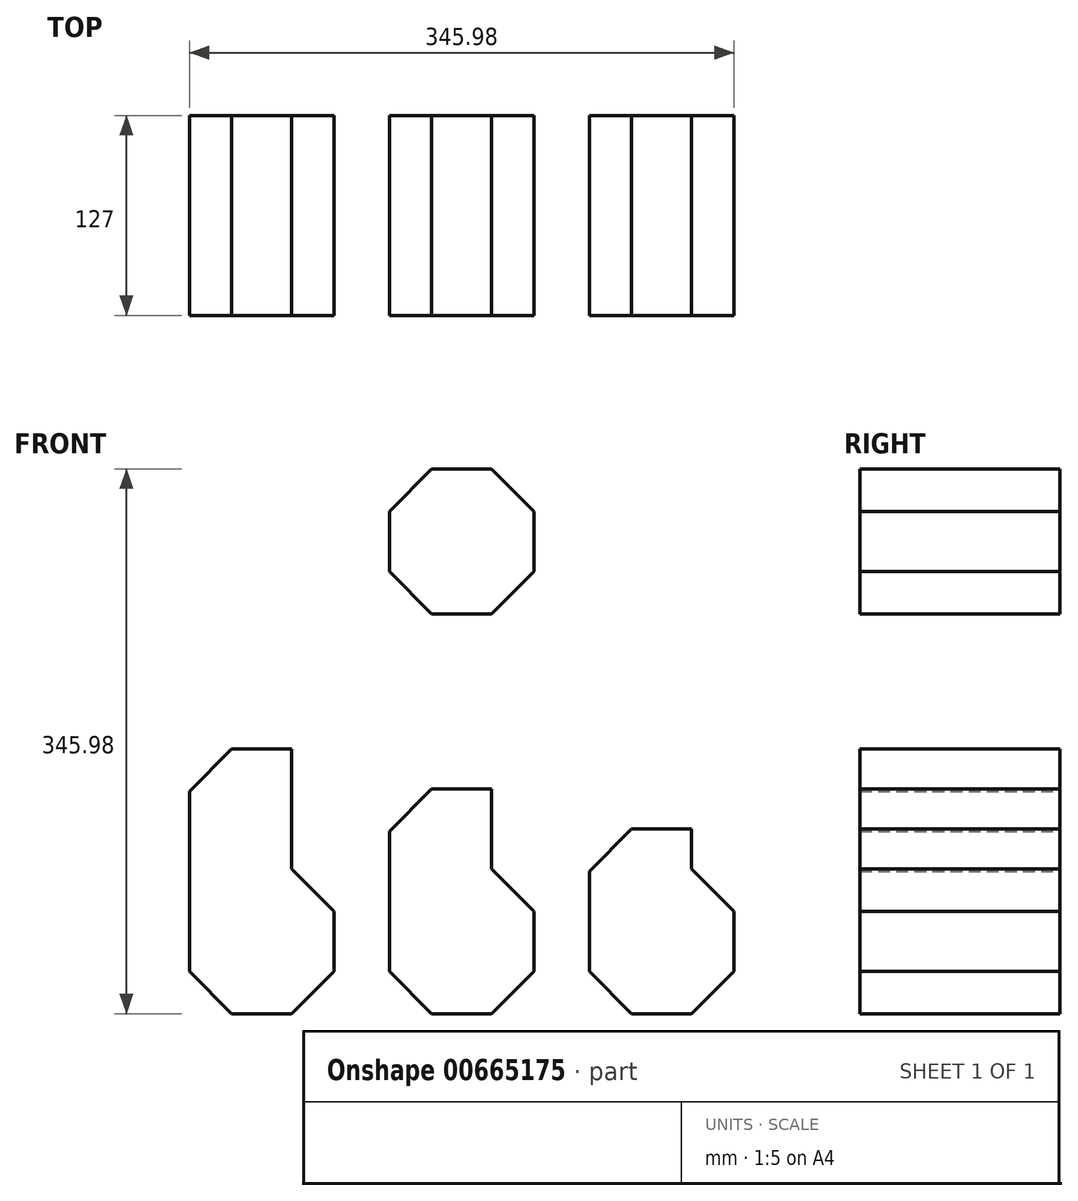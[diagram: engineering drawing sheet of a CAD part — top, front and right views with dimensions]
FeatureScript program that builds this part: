
annotation { "Feature Type Name" : "Feature", "Feature Type Description" : "" }
export const myFeature = defineFeature(function(context is Context, id is Id, definition is map)
    precondition{}
    {
        {
            var Q0;
            Q0=qCreatedBy(makeId("Front.planeOp"),FACE);
            var sketch = newSketch(context, id + "F0", { "sketchPlane" : qUnion([Q0])});
            skCircle(sketch, "E0.cCircle", {"center": v(0, 0) * mm, "radius": 46 * mm, "construction": true});
            skLineSegment(sketch, "E0.0", {"start": v(46, 19.05) * mm, "end": v(46, -19.05) * mm});
            skLineSegment(sketch, "E0.1", {"start": v(46, -19.05) * mm, "end": v(19.05, -46) * mm});
            skLineSegment(sketch, "E0.2", {"start": v(19.05, -46) * mm, "end": v(-19.05, -46) * mm});
            skLineSegment(sketch, "E0.3", {"start": v(-19.05, -46) * mm, "end": v(-46, -19.05) * mm});
            skLineSegment(sketch, "E0.4", {"start": v(-46, -19.05) * mm, "end": v(-46, 19.05) * mm});
            skLineSegment(sketch, "E0.5", {"start": v(-46, 19.05) * mm, "end": v(-19.05, 46) * mm});
            skLineSegment(sketch, "E0.6", {"start": v(-19.05, 46) * mm, "end": v(19.05, 46) * mm});
            skLineSegment(sketch, "E0.7", {"start": v(19.05, 46) * mm, "end": v(46, 19.05) * mm});
            skPoint(sketch, "E0.0.midPoint", {"position": v(46, 0) * mm});
            skSolve(sketch);
        }
        {
            var Q0;
            Q0=makeQuery(id+"F0.imprint","IMPRINT",FACE,{"disambiguationData":[TD([[makeQuery(id+"F0.imprint","IMPRINT",EDGE,{"derivedFrom":sQuery(id+"F0.wireOp",EDGE,"E0.0")}),-1.0]])]});
            extrude(context, id + "F1", {"entities" : qUnion([Q0]), "depth" : 127 * mm, "offsetDistance" : 25.4 * mm});
        }
        {
            var Q0;
            Q0=makeQuery(id+"F1.opExtrude","SWEPT_BODY",BODY,{"disambiguationData":[OSD([sQuery(id+"F0.wireOp",EDGE,"E0.0"),sQuery(id+"F0.wireOp",EDGE,"E0.1"),sQuery(id+"F0.wireOp",EDGE,"E0.2"),sQuery(id+"F0.wireOp",EDGE,"E0.3"),sQuery(id+"F0.wireOp",EDGE,"E0.4"),sQuery(id+"F0.wireOp",EDGE,"E0.5"),sQuery(id+"F0.wireOp",EDGE,"E0.6"),sQuery(id+"F0.wireOp",EDGE,"E0.7")])]});
            var Q1;
            Q1=makeQuery(id+"F1.opExtrude","CAP_EDGE",EDGE,{"disambiguationData":[OSD([sQuery(id+"F0.wireOp",EDGE,"E0.4")])],"isStart":false});
            transform(context, id + "F2", {"entities" : qUnion([Q0]), "transformType" : TransformType.TRANSLATION_DISTANCE, "transformDirection" : qUnion([Q1]), "distance" : 254 * mm, "makeCopy" : true});
        }
        {
            var Q0;
            Q0=makeQuery(id+"F1.opExtrude","SWEPT_BODY",BODY,{"disambiguationData":[OSD([sQuery(id+"F0.wireOp",EDGE,"E0.0"),sQuery(id+"F0.wireOp",EDGE,"E0.1"),sQuery(id+"F0.wireOp",EDGE,"E0.2"),sQuery(id+"F0.wireOp",EDGE,"E0.3"),sQuery(id+"F0.wireOp",EDGE,"E0.4"),sQuery(id+"F0.wireOp",EDGE,"E0.5"),sQuery(id+"F0.wireOp",EDGE,"E0.6"),sQuery(id+"F0.wireOp",EDGE,"E0.7")])]});
            var Q1;
            Q1=makeQuery(id+"F1.opExtrude","CAP_EDGE",EDGE,{"disambiguationData":[OSD([sQuery(id+"F0.wireOp",EDGE,"E0.6")])],"isStart":false});
            transform(context, id + "F3", {"entities" : qUnion([Q0]), "transformType" : TransformType.TRANSLATION_DISTANCE, "transformDirection" : qUnion([Q1]), "distance" : 127 * mm, "makeCopy" : true});
        }
        {
            var Q0;
            Q0=makeQuery(id+"F1.opExtrude","SWEPT_BODY",BODY,{"disambiguationData":[OSD([sQuery(id+"F0.wireOp",EDGE,"E0.0"),sQuery(id+"F0.wireOp",EDGE,"E0.1"),sQuery(id+"F0.wireOp",EDGE,"E0.2"),sQuery(id+"F0.wireOp",EDGE,"E0.3"),sQuery(id+"F0.wireOp",EDGE,"E0.4"),sQuery(id+"F0.wireOp",EDGE,"E0.5"),sQuery(id+"F0.wireOp",EDGE,"E0.6"),sQuery(id+"F0.wireOp",EDGE,"E0.7")])]});
            var Q1;
            Q1=makeQuery(id+"F1.opExtrude","CAP_EDGE",EDGE,{"disambiguationData":[OSD([sQuery(id+"F0.wireOp",EDGE,"E0.6")])],"isStart":false});
            var Q2;
            Q2=makeQuery(id+"F1.opExtrude","CAP_EDGE",EDGE,{"disambiguationData":[OSD([sQuery(id+"F0.wireOp",EDGE,"E0.6")])],"isStart":false});
            transform(context, id + "F4", {"entities" : qUnion([Q0]), "transformType" : TransformType.TRANSLATION_DISTANCE, "transformDirection" : qUnion([Q2]), "distance" : 127 * mm, "oppositeDirection" : true, "makeCopy" : true});
        }
        {
            var Q0;
            Q0=makeQuery(id+"F4.opPattern","COPY",FACE,{"derivedFrom":makeQuery(id+"F1.opExtrude","SWEPT_FACE",FACE,{"disambiguationData":[OSD([sQuery(id+"F0.wireOp",EDGE,"E0.6")])]}),"instanceName":"1"});
            var Q1;
            Q1=makeQuery(id+"F4.opPattern","COPY",FACE,{"derivedFrom":makeQuery(id+"F1.opExtrude","SWEPT_FACE",FACE,{"disambiguationData":[OSD([sQuery(id+"F0.wireOp",EDGE,"E0.5")])]}),"instanceName":"1"});
            extrude(context, id + "F5", {"entities" : qUnion([Q0, Q1]), "operationType" : NewBodyOperationType.ADD, "depth" : 76.2 * mm, "offsetDistance" : 25.4 * mm});
        }
        {
            var Q0;
            Q0=makeQuery(id+"F1.opExtrude","SWEPT_FACE",FACE,{"disambiguationData":[OSD([sQuery(id+"F0.wireOp",EDGE,"E0.6")])]});
            var Q1;
            Q1=makeQuery(id+"F1.opExtrude","SWEPT_FACE",FACE,{"disambiguationData":[OSD([sQuery(id+"F0.wireOp",EDGE,"E0.5")])]});
            extrude(context, id + "F6", {"entities" : qUnion([Q0, Q1]), "operationType" : NewBodyOperationType.ADD, "depth" : 50.8 * mm, "offsetDistance" : 25.4 * mm});
        }
        {
            var Q0;
            Q0=makeQuery(id+"F3.opPattern","COPY",FACE,{"derivedFrom":makeQuery(id+"F1.opExtrude","SWEPT_FACE",FACE,{"disambiguationData":[OSD([sQuery(id+"F0.wireOp",EDGE,"E0.6")])]}),"instanceName":"1"});
            var Q1;
            Q1=makeQuery(id+"F3.opPattern","COPY",FACE,{"derivedFrom":makeQuery(id+"F1.opExtrude","SWEPT_FACE",FACE,{"disambiguationData":[OSD([sQuery(id+"F0.wireOp",EDGE,"E0.5")])]}),"instanceName":"1"});
            extrude(context, id + "F7", {"entities" : qUnion([Q0, Q1]), "operationType" : NewBodyOperationType.ADD, "depth" : 25.4 * mm, "offsetDistance" : 25.4 * mm});
        }
    });
